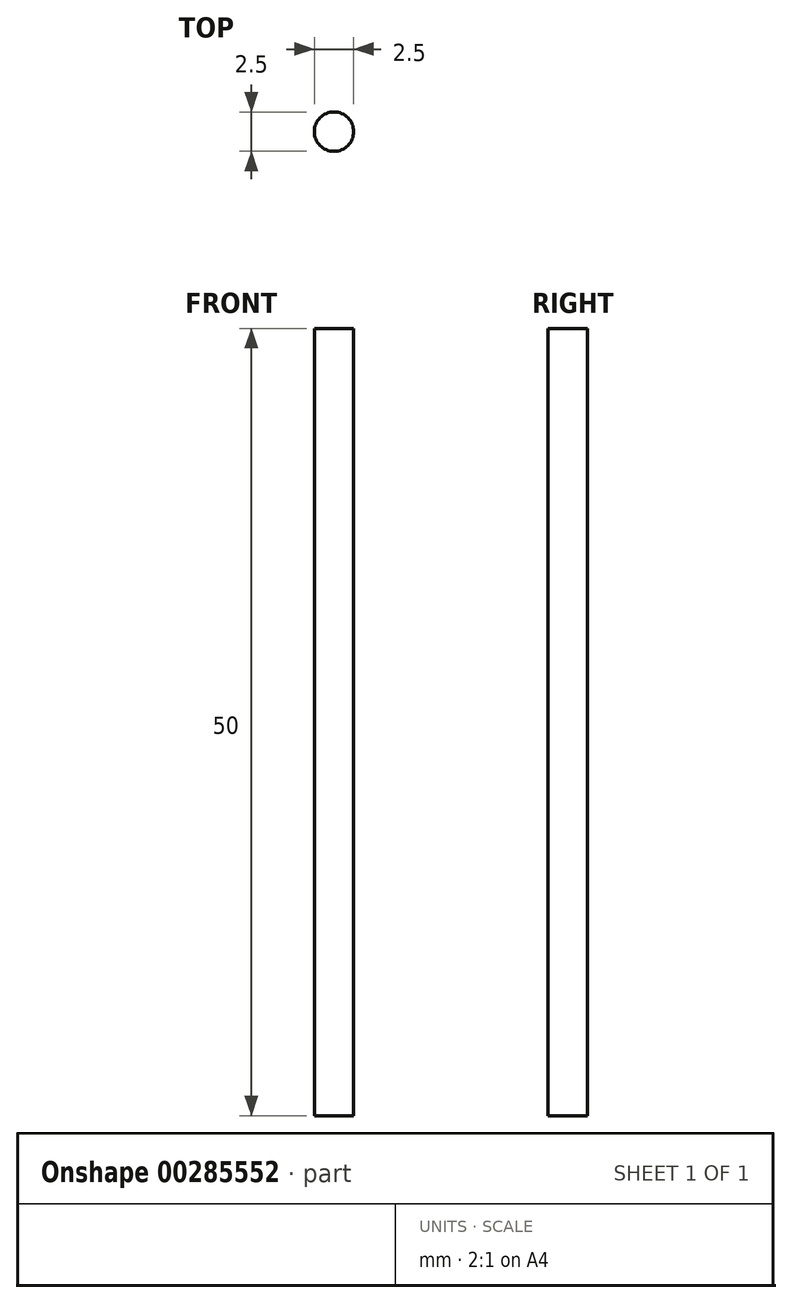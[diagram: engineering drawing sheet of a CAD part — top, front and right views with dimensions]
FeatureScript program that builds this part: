
annotation { "Feature Type Name" : "Feature", "Feature Type Description" : "" }
export const myFeature = defineFeature(function(context is Context, id is Id, definition is map)
    precondition{}
    {
        {
            var Q0;
            Q0=qCreatedBy(makeId("Top.planeOp"),FACE);
            var sketch = newSketch(context, id + "F0", { "sketchPlane" : qUnion([Q0])});
            skCircle(sketch, "E0", {"center": v(0, 0) * mm, "radius": 1.25 * mm});
            skSolve(sketch);
        }
        {
            var Q0;
            Q0 = qSketchRegion(id + "F0", true);
            extrude(context, id + "F1", {"entities" : qUnion([Q0]), "depth" : 50 * mm});
        }
    });
